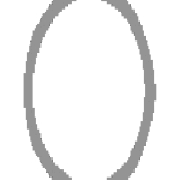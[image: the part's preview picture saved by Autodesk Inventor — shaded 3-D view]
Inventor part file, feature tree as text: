
AUTODESK INVENTOR PART (.ipt)
format: ipt  version: 2021 (Build 250183000, 183)  size: 109,568 bytes
history: native  units: in
note: dims shown in document units (in); Inventor stores cm internally (conversion verified against a paired STEP export)
features: other x4, sketch x3, plane x1
ambient origin geometry x8: Origin, YZ Plane, XZ Plane, XY Plane, X Axis, Y Axis, Z Axis, Center Point
bodies: Solid1 (feature_tree), Body (feature_tree)
feature tree (8):
  other  "Driven Length"
  other  "Frame Generator"
  other  "Start Plane"
  other  "End Plane"
  sketch  "Sketch"  dims[d2=31.6893in d4=-0.0in d5=31.6893in d6=0.12in d7=0.0in d10=90.0deg d9=31.6893in]
  sketch  "Sketch4"  dims[d0=1.0in]
  plane  "Work Plane4"
  sketch  "Sketch5"  dims[d1=0.065in]
